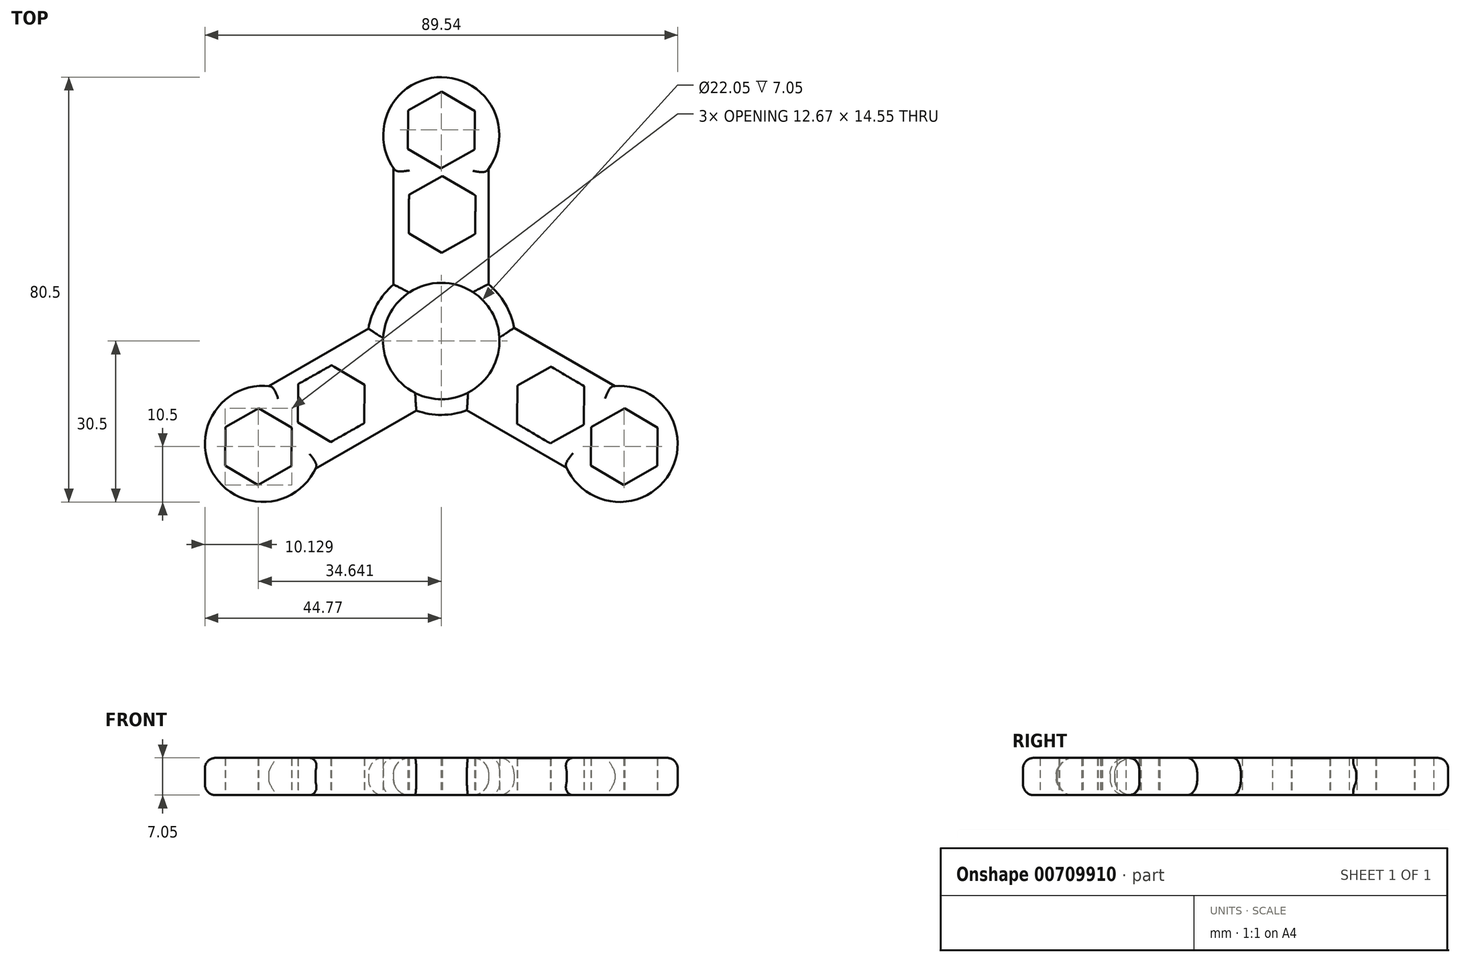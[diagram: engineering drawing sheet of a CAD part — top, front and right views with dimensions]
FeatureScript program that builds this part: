
annotation { "Feature Type Name" : "Feature", "Feature Type Description" : "" }
export const myFeature = defineFeature(function(context is Context, id is Id, definition is map)
    precondition{}
    {
        {
            var Q0;
            Q0=qCreatedBy(makeId("Top.planeOp"),FACE);
            var sketch = newSketch(context, id + "F0", { "sketchPlane" : qUnion([Q0])});
            skCircle(sketch, "E0", {"center": v(0, 0) * mm, "radius": 11.03 * mm});
            skCircle(sketch, "E1", {"center": v(0, 0) * mm, "radius": 14 * mm});
            skLineSegment(sketch, "E2.bottom", {"start": v(-9.05, 39) * mm, "end": v(8.95, 39) * mm});
            skLineSegment(sketch, "E2.top", {"start": v(-9.05, 9) * mm, "end": v(8.95, 9) * mm});
            skLineSegment(sketch, "E2.left", {"start": v(-9.05, 39) * mm, "end": v(-9.05, 9) * mm});
            skLineSegment(sketch, "E2.right", {"start": v(8.95, 39) * mm, "end": v(8.95, 9) * mm});
            skCircle(sketch, "E3", {"center": v(0, 39) * mm, "radius": 11 * mm});
            skCircle(sketch, "E4.cCircle", {"center": v(0, 40) * mm, "radius": 6.3 * mm, "construction": true});
            skLineSegment(sketch, "E4.0", {"start": v(6.26, 36.3) * mm, "end": v(-0.07, 32.73) * mm});
            skLineSegment(sketch, "E4.1", {"start": v(-0.07, 32.73) * mm, "end": v(-6.33, 36.42) * mm});
            skLineSegment(sketch, "E4.2", {"start": v(-6.33, 36.42) * mm, "end": v(-6.26, 43.7) * mm});
            skLineSegment(sketch, "E4.3", {"start": v(-6.26, 43.7) * mm, "end": v(0.07, 47.27) * mm});
            skLineSegment(sketch, "E4.4", {"start": v(0.07, 47.27) * mm, "end": v(6.33, 43.58) * mm});
            skLineSegment(sketch, "E4.5", {"start": v(6.33, 43.58) * mm, "end": v(6.26, 36.3) * mm});
            skPoint(sketch, "E4.0.midPoint", {"position": v(3.1, 34.51) * mm});
            skCircle(sketch, "E5.cCircle", {"center": v(0.15, 24) * mm, "radius": 6.3 * mm, "construction": true});
            skLineSegment(sketch, "E5.0", {"start": v(6.42, 20.3) * mm, "end": v(0.08, 16.73) * mm});
            skLineSegment(sketch, "E5.1", {"start": v(0.08, 16.73) * mm, "end": v(-6.18, 20.42) * mm});
            skLineSegment(sketch, "E5.2", {"start": v(-6.18, 20.42) * mm, "end": v(-6.11, 27.7) * mm});
            skLineSegment(sketch, "E5.3", {"start": v(-6.11, 27.7) * mm, "end": v(0.22, 31.27) * mm});
            skLineSegment(sketch, "E5.4", {"start": v(0.22, 31.27) * mm, "end": v(6.49, 27.58) * mm});
            skLineSegment(sketch, "E5.5", {"start": v(6.49, 27.58) * mm, "end": v(6.42, 20.3) * mm});
            skPoint(sketch, "E5.0.midPoint", {"position": v(3.25, 18.51) * mm});
            skSolve(sketch);
        }
        {
            var Q0;
            {var subQ6=sQuery(id+"F0.wireOp",EDGE,"E4.3");Q0=makeQuery(id+"F0.imprint","IMPRINT",FACE,{"disambiguationData":[TD([[makeQuery(id+"F0.imprint","IMPRINT",EDGE,{"derivedFrom":subQ6}),1.0]])]});}
            var Q1;
            {var subQ10=sQuery(id+"F0.wireOp",EDGE,"E4.0");Q1=makeQuery(id+"F0.imprint","IMPRINT",FACE,{"disambiguationData":[TD([[makeQuery(id+"F0.imprint","IMPRINT",EDGE,{"derivedFrom":subQ10}),1.0]])]});}
            var Q2;
            Q2=makeQuery(id+"F0.imprint","IMPRINT",FACE,{"disambiguationData":[TD([[makeQuery(id+"F0.imprint","IMPRINT",EDGE,{"derivedFrom":sQuery(id+"F0.wireOp",EDGE,"E5.0")}),1.0]])]});
            var Q3;
            {var subQ1=sQuery(id+"F0.wireOp",EDGE,"E2.top");var subQ3=sQuery(id+"F0.wireOp",EDGE,"E0");var subQ4=makeQuery(id+"F0.imprint","INTERSECT",VERTEX,{"disambiguationData":[OD(0.0)],"derivedFrom":[subQ3,subQ1]});Q3=makeQuery(id+"F0.imprint","IMPRINT",FACE,{"disambiguationData":[TD([[makeQuery(id+"F0.imprint","IMPRINT",EDGE,{"disambiguationData":[TD([[subQ4,1.0]])],"derivedFrom":subQ3}),-1.0]])]});}
            var Q4;
            {var subQ1=sQuery(id+"F0.wireOp",EDGE,"E2.top");var subQ3=sQuery(id+"F0.wireOp",EDGE,"E0");var subQ7=makeQuery(id+"F0.imprint","INTERSECT",VERTEX,{"disambiguationData":[OD(0.0)],"derivedFrom":[subQ3,subQ1]});Q4=makeQuery(id+"F0.imprint","IMPRINT",FACE,{"disambiguationData":[TD([[makeQuery(id+"F0.imprint","IMPRINT",EDGE,{"disambiguationData":[TD([[subQ7,-1.0]])],"derivedFrom":subQ3}),-1.0]])]});}
            extrude(context, id + "F1", {"entities" : qUnion([Q0, Q1, Q2, Q3, Q4]), "depth" : 7.05 * mm, "offsetDistance" : 25 * mm});
        }
        {
            var Q0;
            Q0=makeQuery(id+"F1.opExtrude","SWEPT_BODY",BODY,{"disambiguationData":[OSD([sQuery(id+"F0.wireOp",EDGE,"E0"),sQuery(id+"F0.wireOp",EDGE,"E1"),sQuery(id+"F0.wireOp",EDGE,"E2.bottom"),sQuery(id+"F0.wireOp",EDGE,"E2.left"),sQuery(id+"F0.wireOp",EDGE,"E2.right"),sQuery(id+"F0.wireOp",EDGE,"E3"),sQuery(id+"F0.wireOp",EDGE,"E4.0"),sQuery(id+"F0.wireOp",EDGE,"E4.1"),sQuery(id+"F0.wireOp",EDGE,"E4.2"),sQuery(id+"F0.wireOp",EDGE,"E4.3"),sQuery(id+"F0.wireOp",EDGE,"E4.4"),sQuery(id+"F0.wireOp",EDGE,"E4.5"),sQuery(id+"F0.wireOp",EDGE,"E5.0"),sQuery(id+"F0.wireOp",EDGE,"E5.1"),sQuery(id+"F0.wireOp",EDGE,"E5.2"),sQuery(id+"F0.wireOp",EDGE,"E5.3"),sQuery(id+"F0.wireOp",EDGE,"E5.4"),sQuery(id+"F0.wireOp",EDGE,"E5.5")])]});
            var Q1;
            Q1=makeQuery(id+"F1.opExtrude","SWEPT_FACE",FACE,{"disambiguationData":[OSD([sQuery(id+"F0.wireOp",EDGE,"E1")])]});
            circularPattern(context, id + "F2", {"entities" : qUnion([Q0]), "axis" : qUnion([Q1]), "angle" : 360 * degree, "instanceCount" : 3, "equalSpace" : true});
        }
        {
            var Q0;
            Q0=makeQuery(id+"F2.opPattern","COPY",BODY,{"derivedFrom":makeQuery(id+"F1.opExtrude","SWEPT_BODY",BODY,{"disambiguationData":[OSD([sQuery(id+"F0.wireOp",EDGE,"E0"),sQuery(id+"F0.wireOp",EDGE,"E1"),sQuery(id+"F0.wireOp",EDGE,"E2.bottom"),sQuery(id+"F0.wireOp",EDGE,"E2.left"),sQuery(id+"F0.wireOp",EDGE,"E2.right"),sQuery(id+"F0.wireOp",EDGE,"E3"),sQuery(id+"F0.wireOp",EDGE,"E4.0"),sQuery(id+"F0.wireOp",EDGE,"E4.1"),sQuery(id+"F0.wireOp",EDGE,"E4.2"),sQuery(id+"F0.wireOp",EDGE,"E4.3"),sQuery(id+"F0.wireOp",EDGE,"E4.4"),sQuery(id+"F0.wireOp",EDGE,"E4.5"),sQuery(id+"F0.wireOp",EDGE,"E5.0"),sQuery(id+"F0.wireOp",EDGE,"E5.1"),sQuery(id+"F0.wireOp",EDGE,"E5.2"),sQuery(id+"F0.wireOp",EDGE,"E5.3"),sQuery(id+"F0.wireOp",EDGE,"E5.4"),sQuery(id+"F0.wireOp",EDGE,"E5.5")])]}),"instanceName":"2"});
            var Q1;
            Q1=makeQuery(id+"F1.opExtrude","SWEPT_BODY",BODY,{"disambiguationData":[OSD([sQuery(id+"F0.wireOp",EDGE,"E0"),sQuery(id+"F0.wireOp",EDGE,"E1"),sQuery(id+"F0.wireOp",EDGE,"E2.bottom"),sQuery(id+"F0.wireOp",EDGE,"E2.left"),sQuery(id+"F0.wireOp",EDGE,"E2.right"),sQuery(id+"F0.wireOp",EDGE,"E3"),sQuery(id+"F0.wireOp",EDGE,"E4.0"),sQuery(id+"F0.wireOp",EDGE,"E4.1"),sQuery(id+"F0.wireOp",EDGE,"E4.2"),sQuery(id+"F0.wireOp",EDGE,"E4.3"),sQuery(id+"F0.wireOp",EDGE,"E4.4"),sQuery(id+"F0.wireOp",EDGE,"E4.5"),sQuery(id+"F0.wireOp",EDGE,"E5.0"),sQuery(id+"F0.wireOp",EDGE,"E5.1"),sQuery(id+"F0.wireOp",EDGE,"E5.2"),sQuery(id+"F0.wireOp",EDGE,"E5.3"),sQuery(id+"F0.wireOp",EDGE,"E5.4"),sQuery(id+"F0.wireOp",EDGE,"E5.5")])]});
            var Q2;
            Q2=makeQuery(id+"F2.opPattern","COPY",BODY,{"derivedFrom":makeQuery(id+"F1.opExtrude","SWEPT_BODY",BODY,{"disambiguationData":[OSD([sQuery(id+"F0.wireOp",EDGE,"E0"),sQuery(id+"F0.wireOp",EDGE,"E1"),sQuery(id+"F0.wireOp",EDGE,"E2.bottom"),sQuery(id+"F0.wireOp",EDGE,"E2.left"),sQuery(id+"F0.wireOp",EDGE,"E2.right"),sQuery(id+"F0.wireOp",EDGE,"E3"),sQuery(id+"F0.wireOp",EDGE,"E4.0"),sQuery(id+"F0.wireOp",EDGE,"E4.1"),sQuery(id+"F0.wireOp",EDGE,"E4.2"),sQuery(id+"F0.wireOp",EDGE,"E4.3"),sQuery(id+"F0.wireOp",EDGE,"E4.4"),sQuery(id+"F0.wireOp",EDGE,"E4.5"),sQuery(id+"F0.wireOp",EDGE,"E5.0"),sQuery(id+"F0.wireOp",EDGE,"E5.1"),sQuery(id+"F0.wireOp",EDGE,"E5.2"),sQuery(id+"F0.wireOp",EDGE,"E5.3"),sQuery(id+"F0.wireOp",EDGE,"E5.4"),sQuery(id+"F0.wireOp",EDGE,"E5.5")])]}),"instanceName":"1"});
            booleanBodies(context, id + "F3", {"operationType" : BooleanOperationType.UNION, "tools" : qUnion([Q0, Q1, Q2])});
        }
        {
            var Q0;
            Q0=makeQuery(id+"F1.opExtrude","CAP_EDGE",EDGE,{"disambiguationData":[OSD([sQuery(id+"F0.wireOp",EDGE,"E2.left")])],"isStart":false});
            var Q1;
            Q1=makeQuery(id+"F1.opExtrude","CAP_EDGE",EDGE,{"disambiguationData":[OSD([sQuery(id+"F0.wireOp",EDGE,"E2.right")])],"isStart":true});
            var Q2;
            {var subQ0=sQuery(id+"F0.wireOp",EDGE,"E2.right");var subQ2=sQuery(id+"F0.wireOp",EDGE,"E1");Q2=makeQuery(id+"F3.opBoolean","SPLIT",EDGE,{"disambiguationData":[TD([makeQuery(id+"F1.opExtrude","SWEPT_FACE",FACE,{"disambiguationData":[OSD([subQ0])]})])],"derivedFrom":makeQuery(id+"F2.opPattern","COPY",EDGE,{"derivedFrom":makeQuery(id+"F1.opExtrude","CAP_EDGE",EDGE,{"disambiguationData":[OSD([subQ2])],"isStart":false}),"instanceName":"2"})});}
            var Q3;
            {var subQ1=sQuery(id+"F0.wireOp",EDGE,"E2.left");var subQ2=sQuery(id+"F0.wireOp",EDGE,"E1");Q3=makeQuery(id+"F3.opBoolean","SPLIT",EDGE,{"disambiguationData":[TD([makeQuery(id+"F1.opExtrude","SWEPT_FACE",FACE,{"disambiguationData":[OSD([subQ1])]})])],"derivedFrom":makeQuery(id+"F2.opPattern","COPY",EDGE,{"derivedFrom":makeQuery(id+"F1.opExtrude","CAP_EDGE",EDGE,{"disambiguationData":[OSD([subQ2])],"isStart":false}),"instanceName":"2"})});}
            var Q4;
            Q4=makeQuery(id+"F2.opPattern","COPY",EDGE,{"derivedFrom":makeQuery(id+"F1.opExtrude","CAP_EDGE",EDGE,{"disambiguationData":[OSD([sQuery(id+"F0.wireOp",EDGE,"E2.right")])],"isStart":false}),"instanceName":"2"});
            var Q5;
            Q5=makeQuery(id+"F2.opPattern","COPY",EDGE,{"derivedFrom":makeQuery(id+"F1.opExtrude","CAP_EDGE",EDGE,{"disambiguationData":[OSD([sQuery(id+"F0.wireOp",EDGE,"E2.left")])],"isStart":true}),"instanceName":"2"});
            var Q6;
            {var subQ0=sQuery(id+"F0.wireOp",EDGE,"E2.right");var subQ2=sQuery(id+"F0.wireOp",EDGE,"E1");Q6=makeQuery(id+"F3.opBoolean","SPLIT",EDGE,{"disambiguationData":[TD([makeQuery(id+"F2.opPattern","COPY",FACE,{"derivedFrom":makeQuery(id+"F1.opExtrude","SWEPT_FACE",FACE,{"disambiguationData":[OSD([subQ0])]}),"instanceName":"1"})])],"derivedFrom":makeQuery(id+"F2.opPattern","COPY",EDGE,{"derivedFrom":makeQuery(id+"F1.opExtrude","CAP_EDGE",EDGE,{"disambiguationData":[OSD([subQ2])],"isStart":true}),"instanceName":"2"})});}
            var Q7;
            Q7=makeQuery(id+"F2.opPattern","COPY",EDGE,{"derivedFrom":makeQuery(id+"F1.opExtrude","CAP_EDGE",EDGE,{"disambiguationData":[OSD([sQuery(id+"F0.wireOp",EDGE,"E2.right")])],"isStart":true}),"instanceName":"1"});
            var Q8;
            Q8=makeQuery(id+"F2.opPattern","COPY",EDGE,{"derivedFrom":makeQuery(id+"F1.opExtrude","CAP_EDGE",EDGE,{"disambiguationData":[OSD([sQuery(id+"F0.wireOp",EDGE,"E2.left")])],"isStart":false}),"instanceName":"1"});
            var Q9;
            Q9=makeQuery(id+"F2.opPattern","COPY",EDGE,{"derivedFrom":makeQuery(id+"F1.opExtrude","CAP_EDGE",EDGE,{"disambiguationData":[OSD([sQuery(id+"F0.wireOp",EDGE,"E2.left")])],"isStart":false}),"instanceName":"2"});
            var Q10;
            Q10=makeQuery(id+"F2.opPattern","COPY",EDGE,{"derivedFrom":makeQuery(id+"F1.opExtrude","CAP_EDGE",EDGE,{"disambiguationData":[OSD([sQuery(id+"F0.wireOp",EDGE,"E2.right")])],"isStart":false}),"instanceName":"1"});
            var Q11;
            {var subQ0=sQuery(id+"F0.wireOp",EDGE,"E2.right");var subQ2=sQuery(id+"F0.wireOp",EDGE,"E1");Q11=makeQuery(id+"F3.opBoolean","SPLIT",EDGE,{"disambiguationData":[TD([makeQuery(id+"F2.opPattern","COPY",FACE,{"derivedFrom":makeQuery(id+"F1.opExtrude","SWEPT_FACE",FACE,{"disambiguationData":[OSD([subQ0])]}),"instanceName":"1"})])],"derivedFrom":makeQuery(id+"F2.opPattern","COPY",EDGE,{"derivedFrom":makeQuery(id+"F1.opExtrude","CAP_EDGE",EDGE,{"disambiguationData":[OSD([subQ2])],"isStart":false}),"instanceName":"2"})});}
            var Q12;
            Q12=makeQuery(id+"F2.opPattern","COPY",EDGE,{"derivedFrom":makeQuery(id+"F1.opExtrude","CAP_EDGE",EDGE,{"disambiguationData":[OSD([sQuery(id+"F0.wireOp",EDGE,"E2.left")])],"isStart":true}),"instanceName":"1"});
            var Q13;
            {var subQ0=sQuery(id+"F0.wireOp",EDGE,"E2.right");var subQ2=sQuery(id+"F0.wireOp",EDGE,"E1");Q13=makeQuery(id+"F3.opBoolean","SPLIT",EDGE,{"disambiguationData":[TD([makeQuery(id+"F1.opExtrude","SWEPT_FACE",FACE,{"disambiguationData":[OSD([subQ0])]})])],"derivedFrom":makeQuery(id+"F2.opPattern","COPY",EDGE,{"derivedFrom":makeQuery(id+"F1.opExtrude","CAP_EDGE",EDGE,{"disambiguationData":[OSD([subQ2])],"isStart":true}),"instanceName":"2"})});}
            var Q14;
            Q14=makeQuery(id+"F1.opExtrude","CAP_EDGE",EDGE,{"disambiguationData":[OSD([sQuery(id+"F0.wireOp",EDGE,"E2.right")])],"isStart":false});
            var Q15;
            Q15=makeQuery(id+"F1.opExtrude","CAP_EDGE",EDGE,{"disambiguationData":[OSD([sQuery(id+"F0.wireOp",EDGE,"E2.left")])],"isStart":true});
            var Q16;
            {var subQ1=sQuery(id+"F0.wireOp",EDGE,"E2.left");var subQ2=sQuery(id+"F0.wireOp",EDGE,"E1");Q16=makeQuery(id+"F3.opBoolean","SPLIT",EDGE,{"disambiguationData":[TD([makeQuery(id+"F1.opExtrude","SWEPT_FACE",FACE,{"disambiguationData":[OSD([subQ1])]})])],"derivedFrom":makeQuery(id+"F2.opPattern","COPY",EDGE,{"derivedFrom":makeQuery(id+"F1.opExtrude","CAP_EDGE",EDGE,{"disambiguationData":[OSD([subQ2])],"isStart":true}),"instanceName":"2"})});}
            var Q17;
            Q17=makeQuery(id+"F2.opPattern","COPY",EDGE,{"derivedFrom":makeQuery(id+"F1.opExtrude","CAP_EDGE",EDGE,{"disambiguationData":[OSD([sQuery(id+"F0.wireOp",EDGE,"E2.right")])],"isStart":true}),"instanceName":"2"});
            fillet(context, id + "F4", {"entities" : qUnion([Q0, Q1, Q2, Q3, Q4, Q5, Q6, Q7, Q8, Q9, Q10, Q11, Q12, Q13, Q14, Q15, Q16, Q17]), "radius" : 3 * mm, "tangentPropagation" : true, "allowEdgeOverflow" : false});
        }
        {
            var Q0;
            Q0=makeQuery(id+"F1.opExtrude","CAP_EDGE",EDGE,{"disambiguationData":[OSD([sQuery(id+"F0.wireOp",EDGE,"E3")])],"isStart":false});
            var Q1;
            Q1=makeQuery(id+"F2.opPattern","COPY",EDGE,{"derivedFrom":makeQuery(id+"F1.opExtrude","CAP_EDGE",EDGE,{"disambiguationData":[OSD([sQuery(id+"F0.wireOp",EDGE,"E3")])],"isStart":false}),"instanceName":"2"});
            var Q2;
            Q2=makeQuery(id+"F2.opPattern","COPY",EDGE,{"derivedFrom":makeQuery(id+"F1.opExtrude","CAP_EDGE",EDGE,{"disambiguationData":[OSD([sQuery(id+"F0.wireOp",EDGE,"E3")])],"isStart":false}),"instanceName":"1"});
            var Q3;
            Q3=makeQuery(id+"F1.opExtrude","CAP_EDGE",EDGE,{"disambiguationData":[OSD([sQuery(id+"F0.wireOp",EDGE,"E3")])],"isStart":true});
            var Q4;
            Q4=makeQuery(id+"F2.opPattern","COPY",EDGE,{"derivedFrom":makeQuery(id+"F1.opExtrude","CAP_EDGE",EDGE,{"disambiguationData":[OSD([sQuery(id+"F0.wireOp",EDGE,"E3")])],"isStart":true}),"instanceName":"1"});
            var Q5;
            Q5=makeQuery(id+"F2.opPattern","COPY",EDGE,{"derivedFrom":makeQuery(id+"F1.opExtrude","CAP_EDGE",EDGE,{"disambiguationData":[OSD([sQuery(id+"F0.wireOp",EDGE,"E3")])],"isStart":true}),"instanceName":"2"});
            fillet(context, id + "F5", {"entities" : qUnion([Q0, Q1, Q2, Q3, Q4, Q5]), "radius" : 2 * mm, "tangentPropagation" : true, "allowEdgeOverflow" : false});
        }
    });
